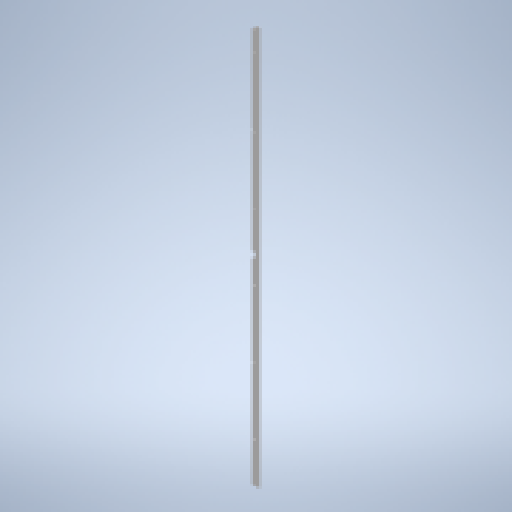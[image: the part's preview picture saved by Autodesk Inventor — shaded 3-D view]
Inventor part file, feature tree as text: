
AUTODESK INVENTOR PART (.ipt)
format: ipt  version: 2025 (Build 290162010, 162A)  size: 383,488 bytes
history: native  units: mm
features: other x4, sketch x4, projected_geometry x3, extrude x2, pattern_linear x2, sheet_metal_op x1
ambient origin geometry x8: Origin, YZ Plane, XZ Plane, XY Plane, X Axis, Y Axis, Z Axis, Center Point
bodies: Body1 (feature_tree)
feature tree (16):
  sheet_metal_op  "Face2"
  other  "Mark1"
  extrude  "Extrusion2"  Depth=2980.0mm
  pattern_linear  "Rectangular Pattern1"  Spacing1=0.0mm  [1 undecoded]
  extrude  "Extrusion3"  Depth=10.0mm
  pattern_linear  "Rectangular Pattern2"  Count1=5  [1 undecoded]
  other  "Corner Chamfer1"
  sketch  "Sketch6"  dims[d26=60.107271mm d27=2980.0mm]
  other  "Plate4"
  sketch  "Sketch7"  dims[d28=3.0mm]
  projected_geometry  "Projected Loop1"
  sketch  "Sketch8"  dims[d29=31.053636mm]
  projected_geometry  "Projected Loop2"
  sketch  "Sketch9"  dims[d30=3.2mm d32=0.0mm d33=0.0mm d34=60.0mm d36=500.0mm d37=50.0mm d38=1490.0mm d39=0.0mm d40=0.0mm d41=20.0mm d43=1480.0mm d44=200.0mm d45=15.0mm d47=10.0mm d48=6.0mm d49=6.0mm d50=45.0deg d51=182.0mm]
  projected_geometry  "Projected Loop3"
  other  "Definition1"
note: 2 required parameter values undecoded (feature->parameter linkage not recoverable at this tier; creation-order binding heuristic only, values carry confidence <= 0.55)
